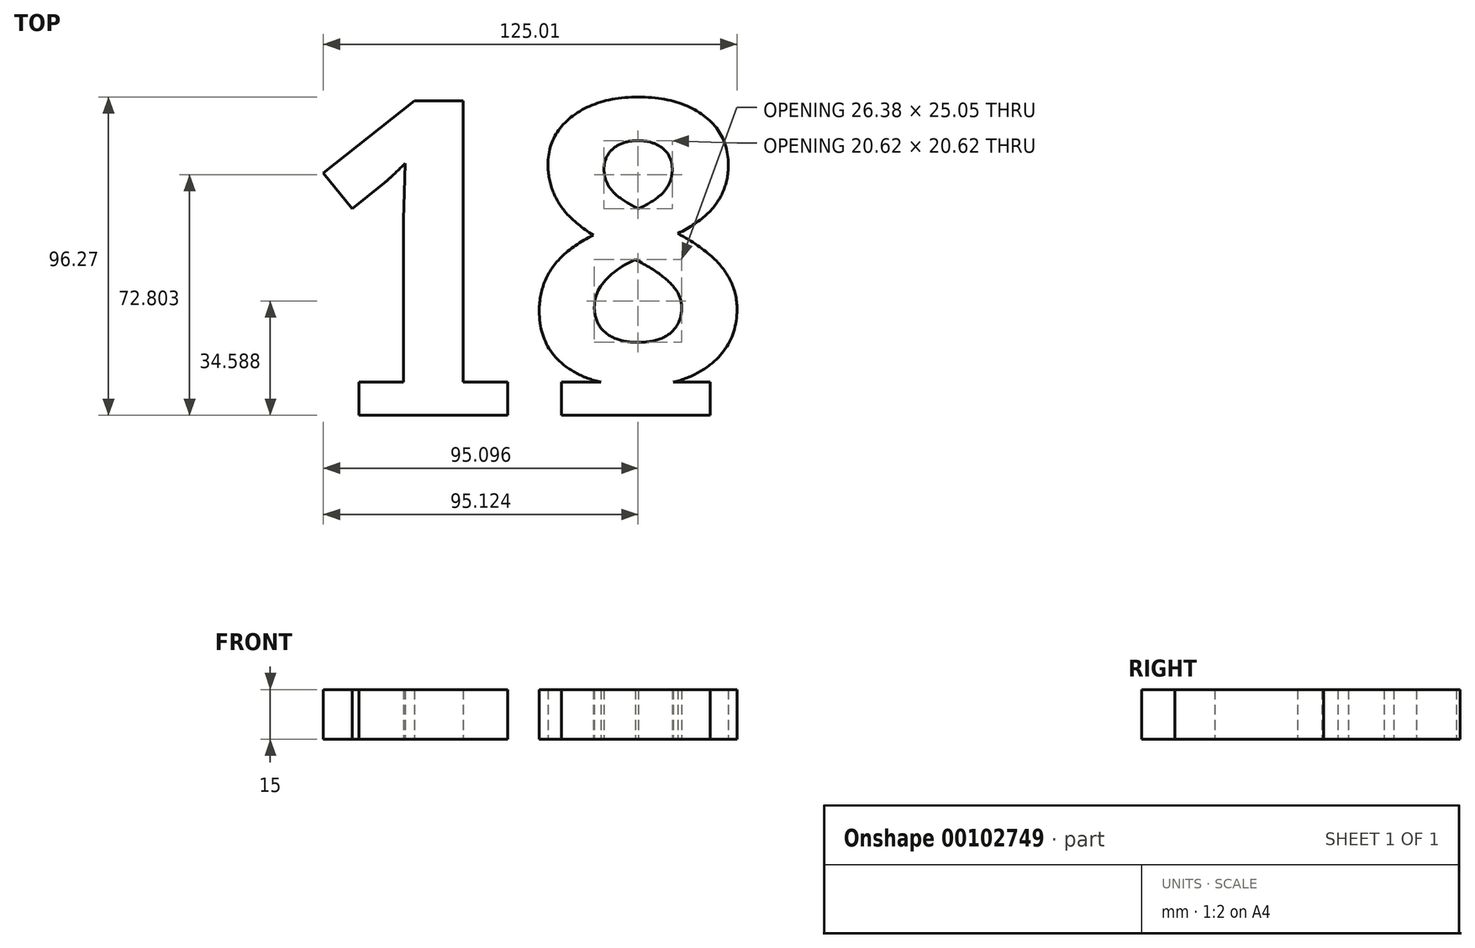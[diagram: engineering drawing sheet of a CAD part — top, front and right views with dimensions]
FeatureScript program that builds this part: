
annotation { "Feature Type Name" : "Feature", "Feature Type Description" : "" }
export const myFeature = defineFeature(function(context is Context, id is Id, definition is map)
    precondition{}
    {
        {
            var Q0;
            Q0=qCreatedBy(makeId("Top.planeOp"),FACE);
            var sketch = newSketch(context, id + "F0", { "sketchPlane" : qUnion([Q0])});
            skText(sketch, "E0", { "text": "18", "fontName": "OpenSans-Bold.ttf"});
            skLineSegment(sketch, "E1.bottom", {"start": v(-35.5, -18.22) * mm, "end": v(9.5, -18.22) * mm});
            skLineSegment(sketch, "E1.top", {"start": v(-35.5, -28.22) * mm, "end": v(9.5, -28.22) * mm});
            skLineSegment(sketch, "E1.left", {"start": v(-35.5, -18.22) * mm, "end": v(-35.5, -28.22) * mm});
            skLineSegment(sketch, "E1.right", {"start": v(9.5, -18.22) * mm, "end": v(9.5, -28.22) * mm});
            skLineSegment(sketch, "E2.bottom", {"start": v(25.72, -18.22) * mm, "end": v(70.72, -18.22) * mm});
            skLineSegment(sketch, "E2.top", {"start": v(25.72, -28.22) * mm, "end": v(70.72, -28.22) * mm});
            skLineSegment(sketch, "E2.left", {"start": v(25.72, -18.22) * mm, "end": v(25.72, -28.22) * mm});
            skLineSegment(sketch, "E2.right", {"start": v(70.72, -18.22) * mm, "end": v(70.72, -28.22) * mm});
            const initialGuessF0  = {"E0": [-0.0533, -0.01822, 1, 0, 0.0859]};
            skSetInitialGuess(sketch, initialGuessF0);
            skSolve(sketch);
        }
        {
            var Q0;
            Q0 = qSketchRegion(id + "F0", true);
            extrude(context, id + "F1", {"entities" : qUnion([Q0]), "depth" : 15 * mm});
        }
    });
